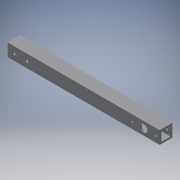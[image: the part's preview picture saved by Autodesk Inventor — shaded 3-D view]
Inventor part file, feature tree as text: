
AUTODESK INVENTOR PART (.ipt)
format: ipt  version: 2016 (Build 200138000, 138)  size: 125,440 bytes
history: native  units: in
note: dims shown in document units (in); Inventor stores cm internally (conversion verified against a paired STEP export)
features: extrude x2, sketch x2
ambient origin geometry x8: Origin, YZ Plane, XZ Plane, XY Plane, X Axis, Y Axis, Z Axis, Center Point
bodies: Solid1 (feature_tree)
feature tree (4):
  extrude  "Extrusion1"  Depth=1.0in
  extrude  "Extrusion2"  Depth=12.0in TaperAngle=0.0deg
  sketch  "Sketch1"  dims[d0=1.0in d1=1.0in]
  sketch  "Sketch2"  dims[d2=0.125in d3=12.0in d4=0.0in d5=1.875in d6=0.5in d7=1.25in d8=0.2in d9=0.2in d10=0.5in d11=1.0in d12=0.0in d13=0.25in d14=0.25in d15=0.5in d16=1.0in]
